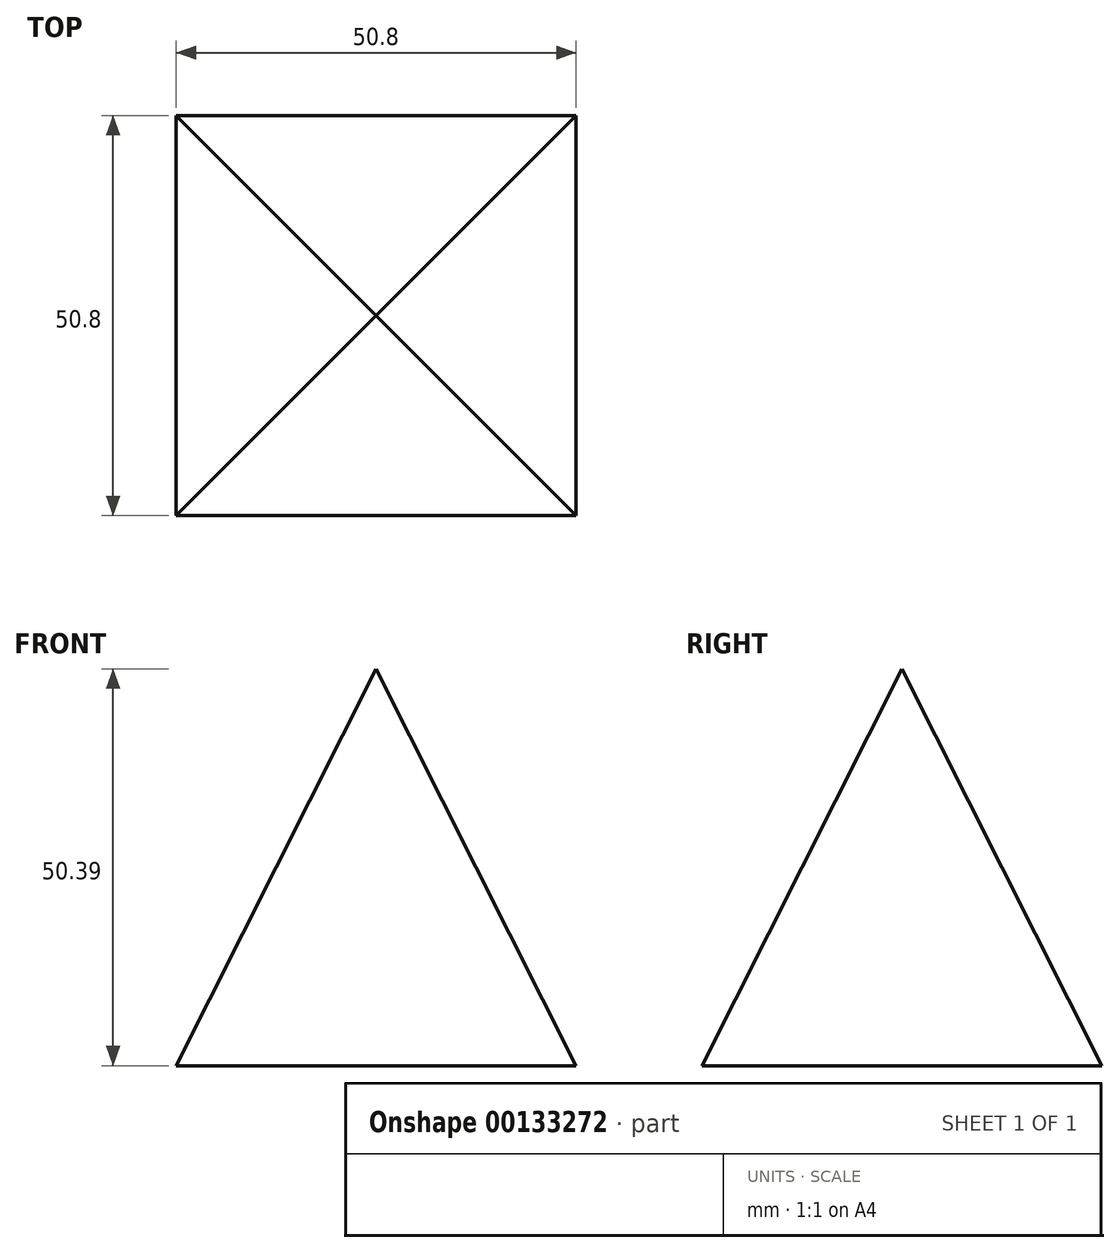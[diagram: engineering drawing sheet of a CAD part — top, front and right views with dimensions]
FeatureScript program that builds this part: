
annotation { "Feature Type Name" : "Feature", "Feature Type Description" : "" }
export const myFeature = defineFeature(function(context is Context, id is Id, definition is map)
    precondition{}
    {
        {
            var Q0;
            Q0=qCreatedBy(makeId("Top.planeOp"),FACE);
            var sketch = newSketch(context, id + "F0", { "sketchPlane" : qUnion([Q0])});
            skLineSegment(sketch, "E0.bottom", {"start": v(-25.4, 25.4) * mm, "end": v(25.4, 25.4) * mm});
            skLineSegment(sketch, "E0.top", {"start": v(-25.4, -25.4) * mm, "end": v(25.4, -25.4) * mm});
            skLineSegment(sketch, "E0.left", {"start": v(-25.4, 25.4) * mm, "end": v(-25.4, -25.4) * mm});
            skLineSegment(sketch, "E0.right", {"start": v(25.4, 25.4) * mm, "end": v(25.4, -25.4) * mm});
            skSolve(sketch);
        }
        {
            var Q0;
            Q0 = qSketchRegion(id + "F0", true);
            extrude(context, id + "F1", {"entities" : qUnion([Q0]), "depth" : 50.8 * mm, "hasDraft" : true, "draftAngle" : 26.75 * degree, "draftPullDirection" : true});
        }
    });
